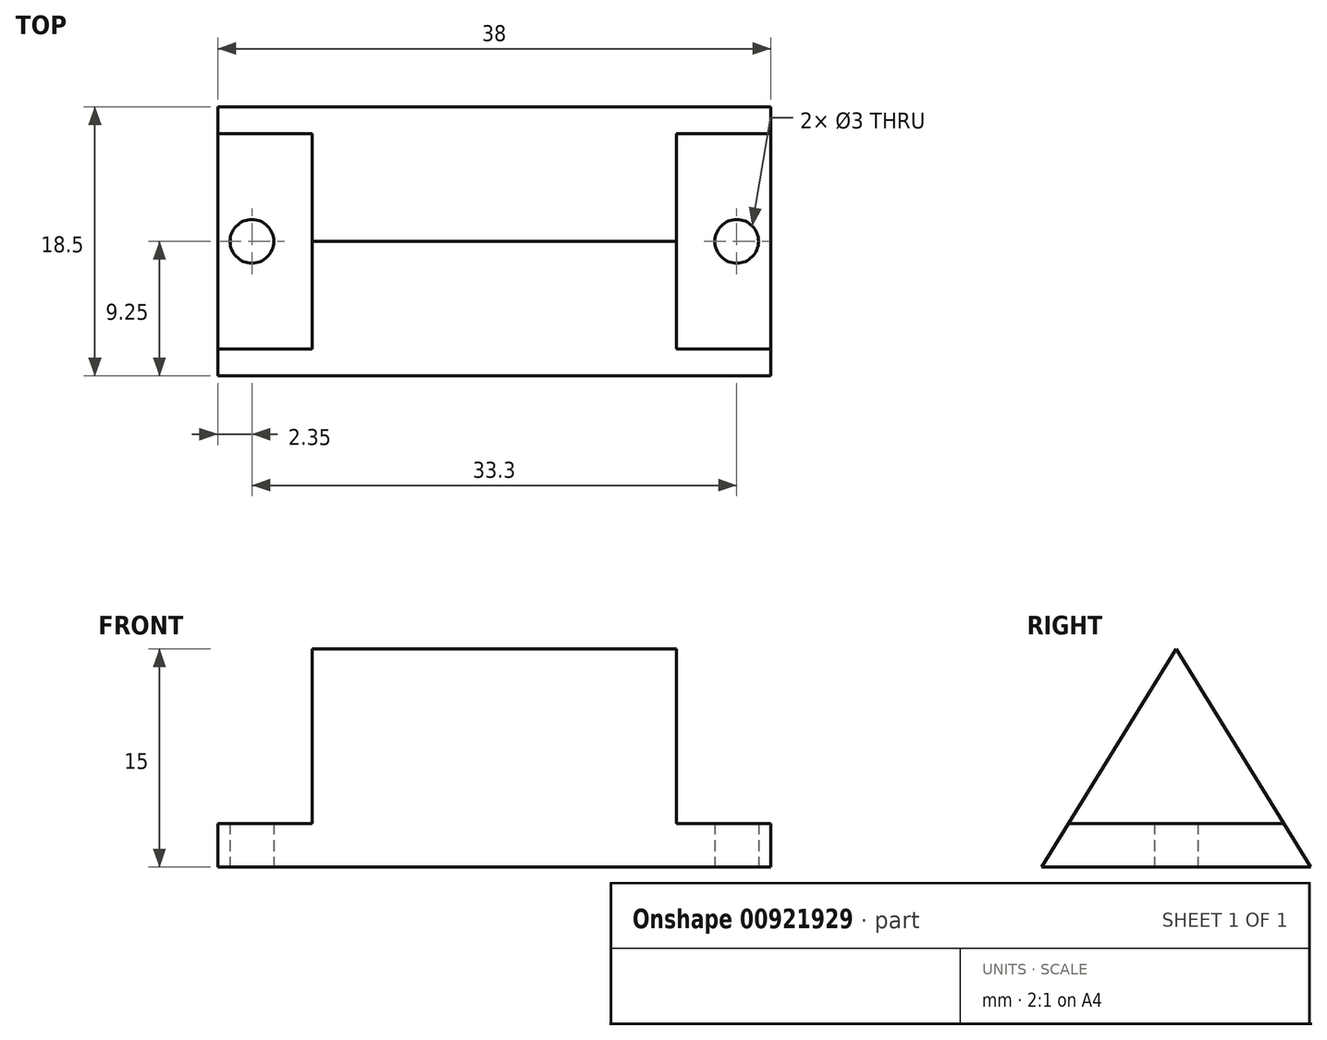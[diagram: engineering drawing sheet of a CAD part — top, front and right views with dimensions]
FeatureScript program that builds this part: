
annotation { "Feature Type Name" : "Feature", "Feature Type Description" : "" }
export const myFeature = defineFeature(function(context is Context, id is Id, definition is map)
    precondition{}
    {
        {
            var Q0;
            Q0=qCreatedBy(makeId("Top.planeOp"),FACE);
            var sketch = newSketch(context, id + "F0", { "sketchPlane" : qUnion([Q0])});
            skLineSegment(sketch, "E0.bottom", {"start": v(19, -9.25) * mm, "end": v(-19, -9.25) * mm});
            skLineSegment(sketch, "E0.top", {"start": v(19, 9.25) * mm, "end": v(-19, 9.25) * mm});
            skLineSegment(sketch, "E0.left", {"start": v(19, -9.25) * mm, "end": v(19, 9.25) * mm});
            skLineSegment(sketch, "E0.right", {"start": v(-19, -9.25) * mm, "end": v(-19, 9.25) * mm});
            skPoint(sketch, "E0.middle", {"position": v(0, 0) * mm});
            skLineSegment(sketch, "E1.bottom", {"start": v(19, -9.25) * mm, "end": v(29, -9.25) * mm});
            skLineSegment(sketch, "E1.top", {"start": v(19, 9.25) * mm, "end": v(29, 9.25) * mm});
            skLineSegment(sketch, "E1.right", {"start": v(29, -9.25) * mm, "end": v(29, 9.25) * mm});
            skLineSegment(sketch, "E2.bottom", {"start": v(-19, -9.25) * mm, "end": v(-29, -9.25) * mm});
            skLineSegment(sketch, "E2.top", {"start": v(-19, 9.25) * mm, "end": v(-29, 9.25) * mm});
            skLineSegment(sketch, "E2.right", {"start": v(-29, -9.25) * mm, "end": v(-29, 9.25) * mm});
            skCircle(sketch, "E3", {"center": v(-25, 0) * mm, "radius": 1.75 * mm});
            skPoint(sketch, "E3.centerSnap0", {"position": v(-29, 0) * mm});
            skCircle(sketch, "E4", {"center": v(25, 0) * mm, "radius": 1.75 * mm});
            skPoint(sketch, "E4.centerSnap0", {"position": v(29, 0) * mm});
            skCircle(sketch, "E5", {"center": v(-16.65, 0) * mm, "radius": 1.5 * mm});
            skCircle(sketch, "E6", {"center": v(16.65, 0) * mm, "radius": 1.5 * mm});
            skSolve(sketch);
        }
        {
            var Q0;
            Q0=makeQuery(id+"F0.imprint","IMPRINT",FACE,{"disambiguationData":[TD([[makeQuery(id+"F0.imprint","IMPRINT",EDGE,{"derivedFrom":sQuery(id+"F0.wireOp",EDGE,"E0.bottom")}),-1.0]])]});
            extrude(context, id + "F1", {"entities" : qUnion([Q0]), "depth" : 15 * mm, "offsetDistance" : 25 * mm});
        }
        {
            var Q0;
            Q0=makeQuery(id+"F1.opExtrude","SWEPT_FACE",FACE,{"disambiguationData":[OSD([sQuery(id+"F0.wireOp",EDGE,"E0.left")])]});
            var sketch = newSketch(context, id + "F2", { "sketchPlane" : qUnion([Q0])});
            skLineSegment(sketch, "E7", {"start": v(-9.25, 0) * mm, "end": v(0, 15) * mm});
            skLineSegment(sketch, "E8", {"start": v(0, 15) * mm, "end": v(9.25, 0) * mm});
            skSolve(sketch);
        }
        {
            var Q0;
            Q0=qSketchRegion(id+"F2",true);
            var Q1;
            {var subQ0=sQuery(id+"F2.wireOp",EDGE,"E7");Q1=makeQuery(id+"F2.imprint","IMPRINT",FACE,{"disambiguationData":[TD([[makeQuery(id+"F2.imprint","IMPRINT",EDGE,{"derivedFrom":subQ0}),1.0]])]});}
            var Q2;
            {var subQ0=sQuery(id+"F2.wireOp",EDGE,"E8");Q2=makeQuery(id+"F2.imprint","IMPRINT",FACE,{"disambiguationData":[TD([[makeQuery(id+"F2.imprint","IMPRINT",EDGE,{"derivedFrom":subQ0}),1.0]])]});}
            extrude(context, id + "F3", {"entities" : qUnion([Q0, Q1, Q2]), "operationType" : NewBodyOperationType.REMOVE, "endBound" : BoundingType.THROUGH_ALL, "oppositeDirection" : true, "depth" : 25 * mm, "offsetDistance" : 25 * mm});
        }
        {
            var Q0;
            Q0=qCreatedBy(makeId("Front.planeOp"),FACE);
            var sketch = newSketch(context, id + "F4", { "sketchPlane" : qUnion([Q0])});
            skLineSegment(sketch, "E9", {"start": v(0, 0) * mm, "end": v(29, 0) * mm, "construction": true});
            skLineSegment(sketch, "E10", {"start": v(29, 0) * mm, "end": v(12.5, 0) * mm});
            skLineSegment(sketch, "E11", {"start": v(0, 0) * mm, "end": v(-29, 0) * mm, "construction": true});
            skLineSegment(sketch, "E12", {"start": v(-29, 0) * mm, "end": v(-12.5, 0) * mm});
            skLineSegment(sketch, "E13", {"start": v(-12.5, 0) * mm, "end": v(-12.5, 3) * mm});
            skLineSegment(sketch, "E14", {"start": v(-12.5, 3) * mm, "end": v(-29, 3) * mm});
            skLineSegment(sketch, "E15", {"start": v(-29, 3) * mm, "end": v(-29, 0) * mm});
            skLineSegment(sketch, "E16", {"start": v(12.5, 0) * mm, "end": v(12.5, 3) * mm});
            skLineSegment(sketch, "E17", {"start": v(12.5, 3) * mm, "end": v(29, 3) * mm});
            skLineSegment(sketch, "E18", {"start": v(29, 3) * mm, "end": v(29, 0) * mm});
            skLineSegment(sketch, "E19.bottom", {"start": v(-29, 3) * mm, "end": v(29, 3) * mm});
            skLineSegment(sketch, "E19.top", {"start": v(-29, 15) * mm, "end": v(29, 15) * mm});
            skLineSegment(sketch, "E19.left", {"start": v(-29, 3) * mm, "end": v(-29, 15) * mm});
            skLineSegment(sketch, "E19.right", {"start": v(29, 3) * mm, "end": v(29, 15) * mm});
            skLineSegment(sketch, "E20", {"start": v(-12.5, 3) * mm, "end": v(-12.5, 15) * mm});
            skLineSegment(sketch, "E21", {"start": v(12.5, 3) * mm, "end": v(12.5, 15) * mm});
            skSolve(sketch);
        }
        {
            var Q0;
            Q0=makeQuery(id+"F4.imprint","IMPRINT",FACE,{"disambiguationData":[TD([[makeQuery(id+"F4.imprint","IMPRINT",EDGE,{"derivedFrom":sQuery(id+"F4.wireOp",EDGE,"E14")}),-1.0]])]});
            var Q1;
            Q1=makeQuery(id+"F4.imprint","IMPRINT",FACE,{"disambiguationData":[TD([[makeQuery(id+"F4.imprint","IMPRINT",EDGE,{"derivedFrom":sQuery(id+"F4.wireOp",EDGE,"E17")}),1.0]])]});
            extrude(context, id + "F5", {"entities" : qUnion([Q0, Q1]), "operationType" : NewBodyOperationType.REMOVE, "depth" : 25 * mm, "offsetDistance" : 25 * mm, "hasSecondDirection" : true, "secondDirectionOppositeDirection" : true, "secondDirectionDepth" : 25 * mm});
        }
    });
